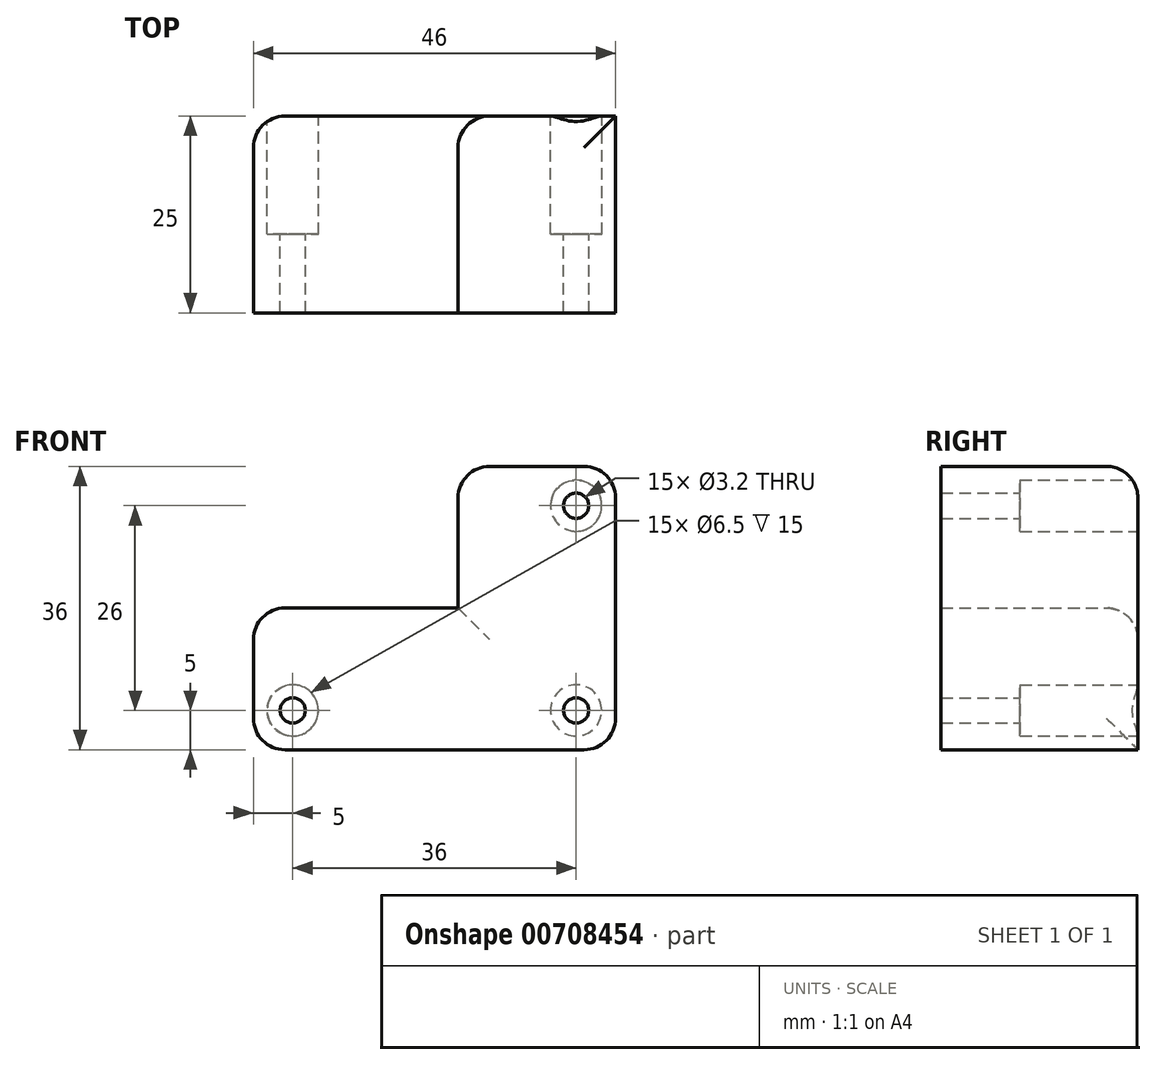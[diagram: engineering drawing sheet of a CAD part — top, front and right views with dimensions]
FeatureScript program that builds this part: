
annotation { "Feature Type Name" : "Feature", "Feature Type Description" : "" }
export const myFeature = defineFeature(function(context is Context, id is Id, definition is map)
    precondition{}
    {
        {
            var Q0;
            Q0=qCreatedBy(makeId("Front.planeOp"),FACE);
            var sketch = newSketch(context, id + "F0", { "sketchPlane" : qUnion([Q0])});
            skPoint(sketch, "E0.middle", {"position": v(0, 0) * mm});
            skLineSegment(sketch, "E1.bottom", {"start": v(-23, -18) * mm, "end": v(23, -18) * mm});
            skLineSegment(sketch, "E1.top", {"start": v(-23, 18) * mm, "end": v(23, 18) * mm});
            skLineSegment(sketch, "E1.left", {"start": v(-23, -18) * mm, "end": v(-23, 18) * mm});
            skLineSegment(sketch, "E1.right", {"start": v(23, -18) * mm, "end": v(23, 18) * mm});
            skLineSegment(sketch, "E2.bottom", {"start": v(-23, 0) * mm, "end": v(3, 0) * mm});
            skLineSegment(sketch, "E2.top", {"start": v(-23, 18) * mm, "end": v(3, 18) * mm});
            skLineSegment(sketch, "E2.left", {"start": v(-23, 0) * mm, "end": v(-23, 18) * mm});
            skLineSegment(sketch, "E2.right", {"start": v(3, 0) * mm, "end": v(3, 18) * mm});
            skCircle(sketch, "E3", {"center": v(-18, -13) * mm, "radius": 1.6 * mm});
            skCircle(sketch, "E4", {"center": v(18, -13) * mm, "radius": 1.6 * mm});
            skCircle(sketch, "E5", {"center": v(18, 13) * mm, "radius": 1.6 * mm});
            skCircle(sketch, "E6", {"center": v(18, 13) * mm, "radius": 3.25 * mm});
            skCircle(sketch, "E7", {"center": v(18, -13) * mm, "radius": 3.25 * mm});
            skCircle(sketch, "E8", {"center": v(-18, -13) * mm, "radius": 3.25 * mm});
            skSolve(sketch);
        }
        {
            var Q0;
            Q0=makeQuery(id+"F0.imprint","IMPRINT",FACE,{"disambiguationData":[TD([[makeQuery(id+"F0.imprint","IMPRINT",EDGE,{"derivedFrom":sQuery(id+"F0.wireOp",EDGE,"E1.bottom")}),1.0]])]});
            var Q1;
            Q1=makeQuery(id+"F0.imprint","IMPRINT",FACE,{"disambiguationData":[TD([[makeQuery(id+"F0.imprint","IMPRINT",EDGE,{"derivedFrom":sQuery(id+"F0.wireOp",EDGE,"E5")}),-1.0]])]});
            var Q2;
            Q2=makeQuery(id+"F0.imprint","IMPRINT",FACE,{"disambiguationData":[TD([[makeQuery(id+"F0.imprint","IMPRINT",EDGE,{"derivedFrom":sQuery(id+"F0.wireOp",EDGE,"E4")}),-1.0]])]});
            var Q3;
            Q3=makeQuery(id+"F0.imprint","IMPRINT",FACE,{"disambiguationData":[TD([[makeQuery(id+"F0.imprint","IMPRINT",EDGE,{"derivedFrom":sQuery(id+"F0.wireOp",EDGE,"E3")}),-1.0]])]});
            extrude(context, id + "F1", {"entities" : qUnion([Q0, Q1, Q2, Q3]), "depth" : 25 * mm, "offsetDistance" : 25 * mm});
        }
        {
            var Q0;
            Q0=makeQuery(id+"F0.imprint","IMPRINT",FACE,{"disambiguationData":[TD([[makeQuery(id+"F0.imprint","IMPRINT",EDGE,{"derivedFrom":sQuery(id+"F0.wireOp",EDGE,"E4")}),-1.0]])]});
            var Q1;
            Q1=makeQuery(id+"F0.imprint","IMPRINT",FACE,{"disambiguationData":[TD([[makeQuery(id+"F0.imprint","IMPRINT",EDGE,{"derivedFrom":sQuery(id+"F0.wireOp",EDGE,"E3")}),-1.0]])]});
            var Q2;
            Q2=makeQuery(id+"F0.imprint","IMPRINT",FACE,{"disambiguationData":[TD([[makeQuery(id+"F0.imprint","IMPRINT",EDGE,{"derivedFrom":sQuery(id+"F0.wireOp",EDGE,"E5")}),-1.0]])]});
            extrude(context, id + "F2", {"entities" : qUnion([Q0, Q1, Q2]), "operationType" : NewBodyOperationType.REMOVE, "depth" : 15 * mm, "offsetDistance" : 25 * mm});
        }
        {
            var Q0;
            Q0=makeQuery(id+"F1.opExtrude","CAP_EDGE",EDGE,{"disambiguationData":[OSD([sQuery(id+"F0.wireOp",EDGE,"E1.left")])],"isStart":true});
            var Q1;
            Q1=makeQuery(id+"F1.opExtrude","CAP_EDGE",EDGE,{"disambiguationData":[OSD([sQuery(id+"F0.wireOp",EDGE,"E2.bottom")])],"isStart":true});
            var Q2;
            Q2=makeQuery(id+"F1.opExtrude","CAP_EDGE",EDGE,{"disambiguationData":[OSD([sQuery(id+"F0.wireOp",EDGE,"E2.right")])],"isStart":true});
            var Q3;
            Q3=makeQuery(id+"F1.opExtrude","CAP_EDGE",EDGE,{"disambiguationData":[OSD([sQuery(id+"F0.wireOp",EDGE,"E1.top")])],"isStart":true});
            var Q4;
            Q4=makeQuery(id+"F1.opExtrude","SWEPT_EDGE",EDGE,{"disambiguationData":[OSD([sQuery(id+"F0.wireOp",EDGE,"E1.left"),sQuery(id+"F0.wireOp",EDGE,"E2.bottom"),sQuery(id+"F0.wireOp",EDGE,"E2.left")])]});
            var Q5;
            Q5=makeQuery(id+"F1.opExtrude","SWEPT_EDGE",EDGE,{"disambiguationData":[OSD([sQuery(id+"F0.wireOp",EDGE,"E1.top"),sQuery(id+"F0.wireOp",EDGE,"E2.top"),sQuery(id+"F0.wireOp",EDGE,"E2.right")])]});
            var Q6;
            Q6=makeQuery(id+"F1.opExtrude","SWEPT_EDGE",EDGE,{"disambiguationData":[OSD([sQuery(id+"F0.wireOp",EDGE,"E1.bottom"),sQuery(id+"F0.wireOp",EDGE,"E1.left")])]});
            var Q7;
            Q7=makeQuery(id+"F1.opExtrude","SWEPT_EDGE",EDGE,{"disambiguationData":[OSD([sQuery(id+"F0.wireOp",EDGE,"E1.bottom"),sQuery(id+"F0.wireOp",EDGE,"E1.right")])]});
            var Q8;
            Q8=makeQuery(id+"F1.opExtrude","SWEPT_EDGE",EDGE,{"disambiguationData":[OSD([sQuery(id+"F0.wireOp",EDGE,"E1.top"),sQuery(id+"F0.wireOp",EDGE,"E1.right")])]});
            fillet(context, id + "F3", {"entities" : qUnion([Q0, Q1, Q2, Q3, Q4, Q5, Q6, Q7, Q8]), "radius" : 4 * mm, "tangentPropagation" : true, "allowEdgeOverflow" : false});
        }
    });
